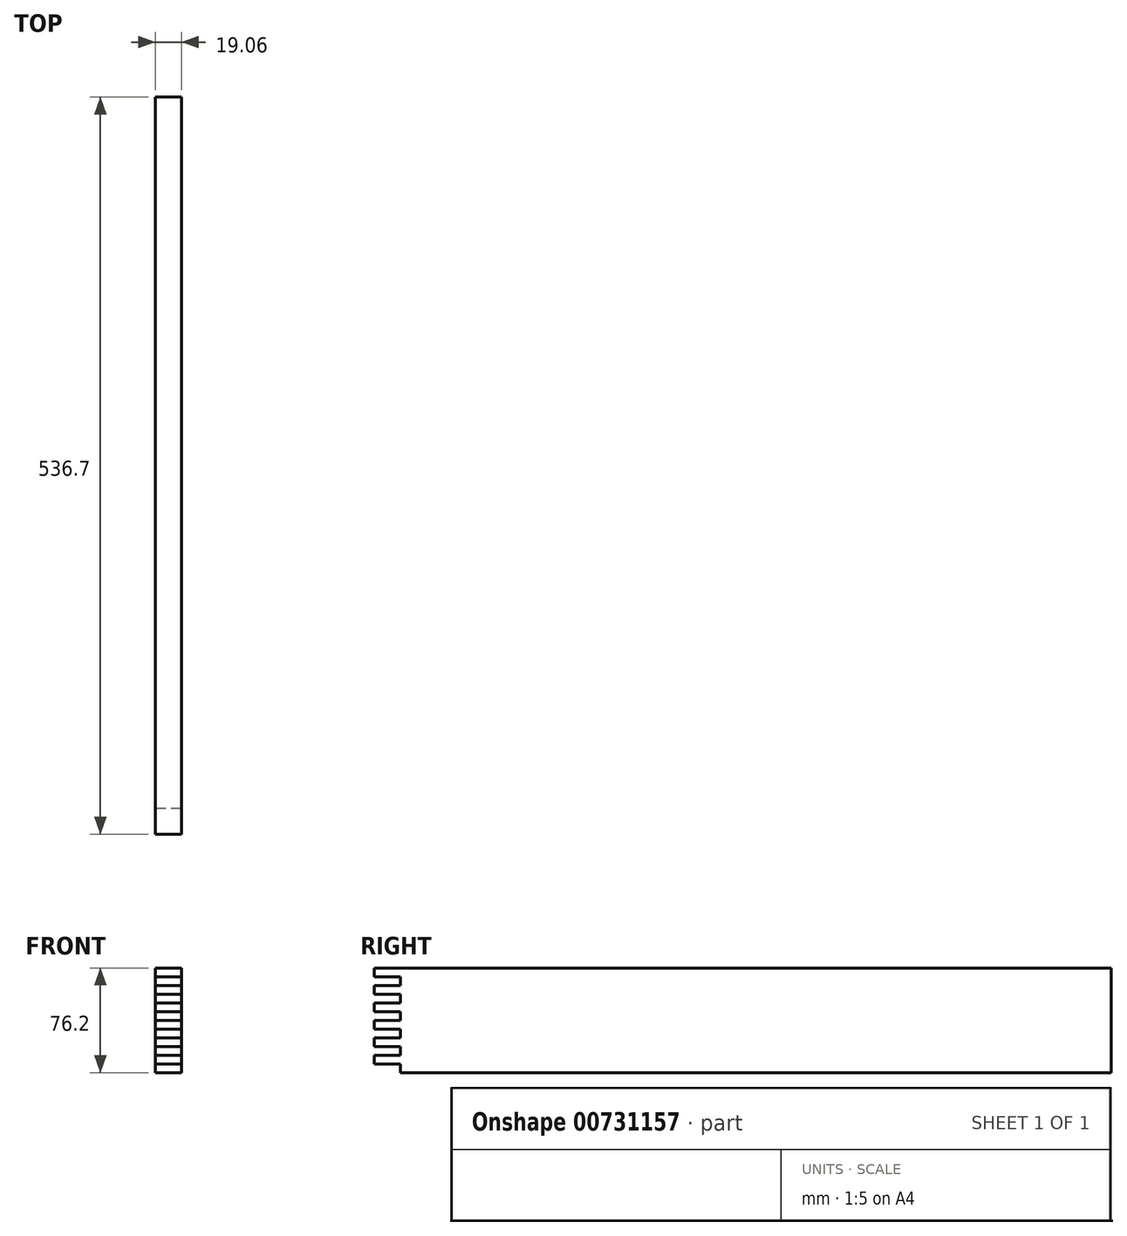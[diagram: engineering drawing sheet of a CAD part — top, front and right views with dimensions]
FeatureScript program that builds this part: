
annotation { "Feature Type Name" : "Feature", "Feature Type Description" : "" }
export const myFeature = defineFeature(function(context is Context, id is Id, definition is map)
    precondition{}
    {
        {
            var Q0;
            Q0=qCreatedBy(makeId("Front.planeOp"),FACE);
            var sketch = newSketch(context, id + "F0", { "sketchPlane" : qUnion([Q0])});
            skLineSegment(sketch, "E0.bottom", {"start": v(9.52, -38.1) * mm, "end": v(-9.53, -38.1) * mm});
            skLineSegment(sketch, "E0.top", {"start": v(9.53, 38.1) * mm, "end": v(-9.52, 38.1) * mm});
            skLineSegment(sketch, "E0.left", {"start": v(9.52, -38.1) * mm, "end": v(9.53, 38.1) * mm});
            skLineSegment(sketch, "E0.right", {"start": v(-9.53, -38.1) * mm, "end": v(-9.52, 38.1) * mm});
            skPoint(sketch, "E0.middle", {"position": v(0, 0) * mm});
            skSolve(sketch);
        }
        {
            var Q0;
            Q0 = qSketchRegion(id + "F0", true);
            extrude(context, id + "F1", {"entities" : qUnion([Q0]), "endBound" : BoundingType.SYMMETRIC, "depth" : 536.7 * mm, "offsetDistance" : 25.4 * mm});
        }
        {
            var Q0;
            Q0=makeQuery(id+"F1.opExtrude","SWEPT_FACE",FACE,{"disambiguationData":[OSD([sQuery(id+"F0.wireOp",EDGE,"E0.left")])]});
            var sketch = newSketch(context, id + "F2", { "sketchPlane" : qUnion([Q0])});
            skLineSegment(sketch, "E1.bottom", {"start": v(-268.35, 31.75) * mm, "end": v(-249.3, 31.75) * mm});
            skLineSegment(sketch, "E1.top", {"start": v(-268.35, 25.4) * mm, "end": v(-249.3, 25.4) * mm});
            skLineSegment(sketch, "E1.left", {"start": v(-268.35, 31.75) * mm, "end": v(-268.35, 25.4) * mm});
            skLineSegment(sketch, "E1.right", {"start": v(-249.3, 31.75) * mm, "end": v(-249.3, 25.4) * mm});
            skLineSegment(sketch, "E2.bottom", {"start": v(-268.35, 6.35) * mm, "end": v(-249.3, 6.35) * mm});
            skLineSegment(sketch, "E2.top", {"start": v(-268.35, 0) * mm, "end": v(-249.3, 0) * mm});
            skLineSegment(sketch, "E2.left", {"start": v(-268.35, 6.35) * mm, "end": v(-268.35, 0) * mm});
            skLineSegment(sketch, "E2.right", {"start": v(-249.3, 6.35) * mm, "end": v(-249.3, 0) * mm});
            skLineSegment(sketch, "E3.bottom", {"start": v(-268.35, -6.35) * mm, "end": v(-249.3, -6.35) * mm});
            skLineSegment(sketch, "E3.top", {"start": v(-268.35, -12.7) * mm, "end": v(-249.3, -12.7) * mm});
            skLineSegment(sketch, "E3.left", {"start": v(-268.35, -6.35) * mm, "end": v(-268.35, -12.7) * mm});
            skLineSegment(sketch, "E3.right", {"start": v(-249.3, -6.35) * mm, "end": v(-249.3, -12.7) * mm});
            skLineSegment(sketch, "E4.bottom", {"start": v(-268.35, -19.05) * mm, "end": v(-249.3, -19.05) * mm});
            skLineSegment(sketch, "E4.top", {"start": v(-268.35, -25.4) * mm, "end": v(-249.3, -25.4) * mm});
            skLineSegment(sketch, "E4.left", {"start": v(-268.35, -19.05) * mm, "end": v(-268.35, -25.4) * mm});
            skLineSegment(sketch, "E4.right", {"start": v(-249.3, -19.05) * mm, "end": v(-249.3, -25.4) * mm});
            skLineSegment(sketch, "E5.bottom", {"start": v(-268.35, 19.05) * mm, "end": v(-249.3, 19.05) * mm});
            skLineSegment(sketch, "E5.top", {"start": v(-268.35, 12.7) * mm, "end": v(-249.3, 12.7) * mm});
            skLineSegment(sketch, "E5.left", {"start": v(-268.35, 19.05) * mm, "end": v(-268.35, 12.7) * mm});
            skLineSegment(sketch, "E5.right", {"start": v(-249.3, 19.05) * mm, "end": v(-249.3, 12.7) * mm});
            skLineSegment(sketch, "E6.bottom", {"start": v(-268.35, -38.1) * mm, "end": v(-249.3, -38.1) * mm});
            skLineSegment(sketch, "E6.top", {"start": v(-268.35, -31.75) * mm, "end": v(-249.3, -31.75) * mm});
            skLineSegment(sketch, "E6.left", {"start": v(-268.35, -38.1) * mm, "end": v(-268.35, -31.75) * mm});
            skLineSegment(sketch, "E6.right", {"start": v(-249.3, -38.1) * mm, "end": v(-249.3, -31.75) * mm});
            skSolve(sketch);
        }
        {
            var Q0;
            Q0 = qSketchRegion(id + "F2", true);
            extrude(context, id + "F3", {"entities" : qUnion([Q0]), "operationType" : NewBodyOperationType.REMOVE, "endBound" : BoundingType.THROUGH_ALL, "oppositeDirection" : true, "depth" : 25.4 * mm, "offsetDistance" : 25.4 * mm});
        }
    });
